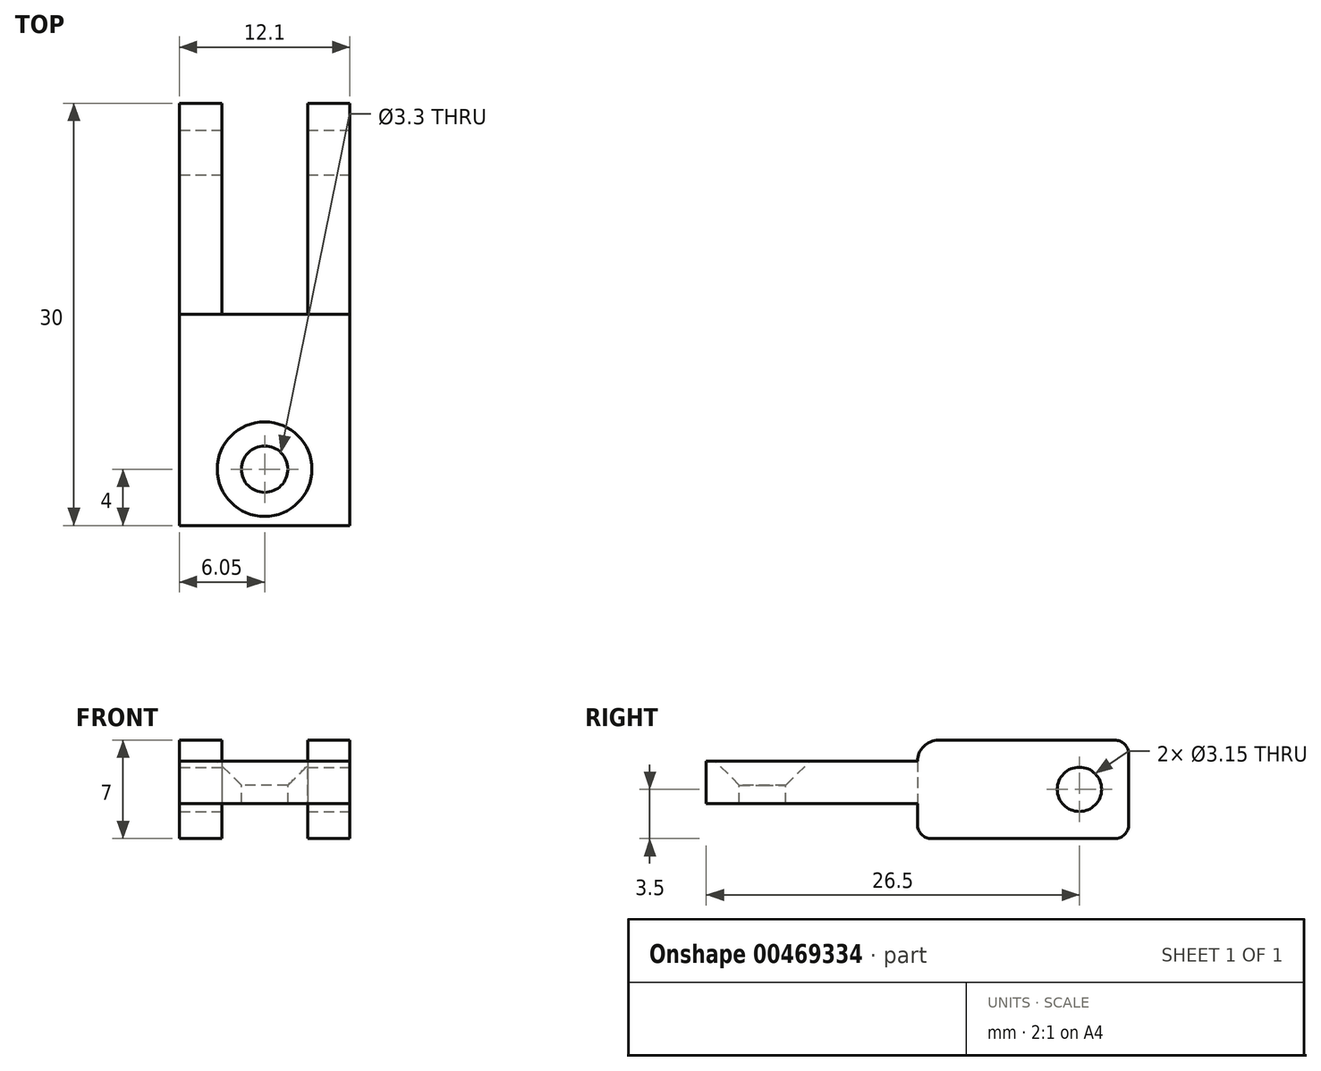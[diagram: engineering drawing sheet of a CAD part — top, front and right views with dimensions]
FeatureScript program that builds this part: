
annotation { "Feature Type Name" : "Feature", "Feature Type Description" : "" }
export const myFeature = defineFeature(function(context is Context, id is Id, definition is map)
    precondition{}
    {
        {
            var Q0;
            Q0=qCreatedBy(makeId("Top.planeOp"),FACE);
            var sketch = newSketch(context, id + "F0", { "sketchPlane" : qUnion([Q0])});
            skLineSegment(sketch, "E0.bottom", {"start": v(0, 0) * mm, "end": v(3.05, 0) * mm});
            skLineSegment(sketch, "E0.top", {"start": v(0, 15) * mm, "end": v(3.05, 15) * mm});
            skLineSegment(sketch, "E0.left", {"start": v(0, 0) * mm, "end": v(0, 15) * mm});
            skLineSegment(sketch, "E0.right", {"start": v(3.05, 0) * mm, "end": v(3.05, 15) * mm});
            skSolve(sketch);
        }
        {
            var Q0;
            Q0=qSketchRegion(id+"F0",true);
            extrude(context, id + "F1", {"entities" : qUnion([Q0]), "depth" : 3 * mm});
        }
        {
            var Q0;
            Q0=makeQuery(id+"F1.opExtrude","SWEPT_FACE",FACE,{"disambiguationData":[OSD([sQuery(id+"F0.wireOp",EDGE,"E0.right")])]});
            var sketch = newSketch(context, id + "F2", { "sketchPlane" : qUnion([Q0])});
            skLineSegment(sketch, "E1", {"start": v(15, 3) * mm, "end": v(15, 3) * mm});
            skLineSegment(sketch, "E2", {"start": v(0, 0) * mm, "end": v(0, 3) * mm});
            skLineSegment(sketch, "E3", {"start": v(30, 4.5) * mm, "end": v(30, -2.5) * mm});
            skLineSegment(sketch, "E4", {"start": v(30, -2.5) * mm, "end": v(15, -2.5) * mm});
            skLineSegment(sketch, "E5", {"start": v(15, -2.5) * mm, "end": v(15, 0) * mm});
            skLineSegment(sketch, "E6", {"start": v(15, 0) * mm, "end": v(0, 0) * mm});
            skPoint(sketch, "E7", {"position": v(30, 1) * mm});
            skLineSegment(sketch, "E8", {"start": v(0, 3) * mm, "end": v(15, 3) * mm});
            skArc(sketch, "E9", {"start": v(15, 3) * mm, "mid": v(15.44, 4.06) * mm, "end": v(16.5, 4.5) * mm});
            skLineSegment(sketch, "E10", {"start": v(30, 4.5) * mm, "end": v(16.5, 4.5) * mm});
            skSolve(sketch);
        }
        {
            var Q0;
            Q0=qSketchRegion(id+"F2",true);
            extrude(context, id + "F3", {"entities" : qUnion([Q0]), "operationType" : NewBodyOperationType.ADD, "depth" : 3 * mm});
        }
        {
            var Q0;
            Q0=makeQuery(id+"F1.opExtrude","SWEPT_BODY",BODY,{"disambiguationData":[OSD([sQuery(id+"F0.wireOp",EDGE,"E0.bottom"),sQuery(id+"F0.wireOp",EDGE,"E0.top"),sQuery(id+"F0.wireOp",EDGE,"E0.left"),sQuery(id+"F0.wireOp",EDGE,"E0.right")])]});
            var Q1;
            Q1=makeQuery(id+"F1.opExtrude","SWEPT_FACE",FACE,{"disambiguationData":[OSD([sQuery(id+"F0.wireOp",EDGE,"E0.left")])]});
            mirror(context, id + "F4", {"operationType" : NewBodyOperationType.ADD, "entities" : qUnion([Q0]), "mirrorPlane" : qUnion([Q1])});
        }
        {
            var Q0;
            {var subQ0=makeQuery(id+"F3.boolean.opBoolean","MERGE",FACE,{"derivedFrom":[makeQuery(id+"F1.opExtrude","CAP_FACE",FACE,{"disambiguationData":[OSD([sQuery(id+"F0.wireOp",EDGE,"E0.bottom"),sQuery(id+"F0.wireOp",EDGE,"E0.top"),sQuery(id+"F0.wireOp",EDGE,"E0.left"),sQuery(id+"F0.wireOp",EDGE,"E0.right")])],"isStart":false}),makeQuery(id+"F3.opExtrude","SWEPT_FACE",FACE,{"disambiguationData":[OSD([sQuery(id+"F2.wireOp",EDGE,"Q6OimDLD-XTNi-JLzE-aSkQ-Egzmejzk890i")])]})]});Q0=makeQuery(id+"F4.boolean.opBoolean","MERGE",FACE,{"derivedFrom":[subQ0,makeQuery(id+"F4.opPattern","COPY",FACE,{"derivedFrom":subQ0,"instanceName":"1"})]});}
            var sketch = newSketch(context, id + "F5", { "sketchPlane" : qUnion([Q0])});
            skLineSegment(sketch, "E11", {"start": v(0, 0) * mm, "end": v(0, 4) * mm, "construction": true});
            skSolve(sketch);
        }
        {
            var Q0;
            Q0=sQuery(id+"F5.wireOp",VERTEX,"E11.end");
            var Q1;
            Q1=makeQuery(id+"F1.opExtrude","SWEPT_BODY",BODY,{"disambiguationData":[OSD([sQuery(id+"F0.wireOp",EDGE,"E0.bottom"),sQuery(id+"F0.wireOp",EDGE,"E0.top"),sQuery(id+"F0.wireOp",EDGE,"E0.left"),sQuery(id+"F0.wireOp",EDGE,"E0.right")])]});
            hole(context, id + "F6", {"style" : HoleStyle.C_SINK, "endStyle" : HoleEndStyle.THROUGH, "standardTappedOrClearance" : lookupTablePath({ "standard" : "ISO", "fit" : "Normal", "size" : "M3", "type" : "Clearance" }), "standardBlindInLast" : lookupTablePath({ "fit" : "Standard", "standard" : "ISO", "size" : "M3", "type" : "Clearance" }), "holeDiameter" : 3.3 * mm, "cSinkDiameter" : 6.72 * mm, "cSinkAngle" : 90 * degree, "isTappedThrough" : true, "tappedDepth" : 12 * mm, "tapClearance" : 3, "locations" : qUnion([Q0]), "scope" : qUnion([Q1])});
        }
        {
            var Q0;
            Q0=makeQuery(id+"F3.opExtrude","CAP_FACE",FACE,{"disambiguationData":[OSD([sQuery(id+"F2.wireOp",EDGE,"E2"),sQuery(id+"F2.wireOp",EDGE,"E3"),sQuery(id+"F2.wireOp",EDGE,"E4"),sQuery(id+"F2.wireOp",EDGE,"E5"),sQuery(id+"F2.wireOp",EDGE,"E6"),sQuery(id+"F2.wireOp",EDGE,"E8"),sQuery(id+"F2.wireOp",EDGE,"E9"),sQuery(id+"F2.wireOp",EDGE,"E10")])],"isStart":false});
            var sketch = newSketch(context, id + "F7", { "sketchPlane" : qUnion([Q0])});
            skLineSegment(sketch, "E12", {"start": v(30, 4.5) * mm, "end": v(23, -2.5) * mm, "construction": true});
            skLineSegment(sketch, "E13", {"start": v(23, -2.5) * mm, "end": v(30, -2.5) * mm, "construction": true});
            skPoint(sketch, "E14", {"position": v(26.5, 1) * mm});
            skSolve(sketch);
        }
        {
            var Q0;
            Q0=sQuery(id+"F7.wireOp",VERTEX,"E14");
            var Q1;
            Q1=makeQuery(id+"F1.opExtrude","SWEPT_BODY",BODY,{"disambiguationData":[OSD([sQuery(id+"F0.wireOp",EDGE,"E0.bottom"),sQuery(id+"F0.wireOp",EDGE,"E0.top"),sQuery(id+"F0.wireOp",EDGE,"E0.left"),sQuery(id+"F0.wireOp",EDGE,"E0.right")])]});
            hole(context, id + "F8", {"style" : HoleStyle.SIMPLE, "endStyle" : HoleEndStyle.THROUGH, "standardTappedOrClearance" : lookupTablePath({ "standard" : "ISO", "fit" : "Close", "size" : "M3", "type" : "Clearance" }), "standardBlindInLast" : lookupTablePath({ "fit" : "Close", "standard" : "ISO", "size" : "M3", "type" : "Clearance" }), "holeDiameter" : 3.15 * mm, "isTappedThrough" : true, "tappedDepth" : 12 * mm, "tapClearance" : 3, "locations" : qUnion([Q0]), "scope" : qUnion([Q1])});
        }
        {
            var Q0;
            Q0=makeQuery(id+"F1.opExtrude","SWEPT_EDGE",EDGE,{"disambiguationData":[OSD([sQuery(id+"F0.wireOp",EDGE,"E0.top"),sQuery(id+"F0.wireOp",EDGE,"E0.right")])]});
            var Q1;
            Q1=makeQuery(id+"F4.opPattern","COPY",EDGE,{"derivedFrom":makeQuery(id+"F1.opExtrude","SWEPT_EDGE",EDGE,{"disambiguationData":[OSD([sQuery(id+"F0.wireOp",EDGE,"E0.top"),sQuery(id+"F0.wireOp",EDGE,"E0.right")])]}),"instanceName":"1"});
            var Q2;
            Q2=makeQuery(id+"F3.opExtrude","SWEPT_EDGE",EDGE,{"disambiguationData":[OSD([sQuery(id+"F2.wireOp",EDGE,"E3"),sQuery(id+"F2.wireOp",EDGE,"E10")])]});
            var Q3;
            Q3=makeQuery(id+"F4.opPattern","COPY",EDGE,{"derivedFrom":makeQuery(id+"F3.opExtrude","SWEPT_EDGE",EDGE,{"disambiguationData":[OSD([sQuery(id+"F2.wireOp",EDGE,"E3"),sQuery(id+"F2.wireOp",EDGE,"E10")])]}),"instanceName":"1"});
            var Q4;
            Q4=makeQuery(id+"F4.opPattern","COPY",EDGE,{"derivedFrom":makeQuery(id+"F3.opExtrude","SWEPT_EDGE",EDGE,{"disambiguationData":[OSD([sQuery(id+"F2.wireOp",EDGE,"E3"),sQuery(id+"F2.wireOp",EDGE,"E4")])]}),"instanceName":"1"});
            var Q5;
            Q5=makeQuery(id+"F3.opExtrude","SWEPT_EDGE",EDGE,{"disambiguationData":[OSD([sQuery(id+"F2.wireOp",EDGE,"E3"),sQuery(id+"F2.wireOp",EDGE,"E4")])]});
            var Q6;
            Q6=makeQuery(id+"F4.opPattern","COPY",EDGE,{"derivedFrom":makeQuery(id+"F3.opExtrude","SWEPT_EDGE",EDGE,{"disambiguationData":[OSD([sQuery(id+"F2.wireOp",EDGE,"E4"),sQuery(id+"F2.wireOp",EDGE,"E5")])]}),"instanceName":"1"});
            var Q7;
            Q7=makeQuery(id+"F3.opExtrude","SWEPT_EDGE",EDGE,{"disambiguationData":[OSD([sQuery(id+"F2.wireOp",EDGE,"E4"),sQuery(id+"F2.wireOp",EDGE,"E5")])]});
            fillet(context, id + "F9", {"entities" : qUnion([Q0, Q1, Q2, Q3, Q4, Q5, Q6, Q7]), "radius" : 1 * mm, "tangentPropagation" : true, "allowEdgeOverflow" : false});
        }
    });
